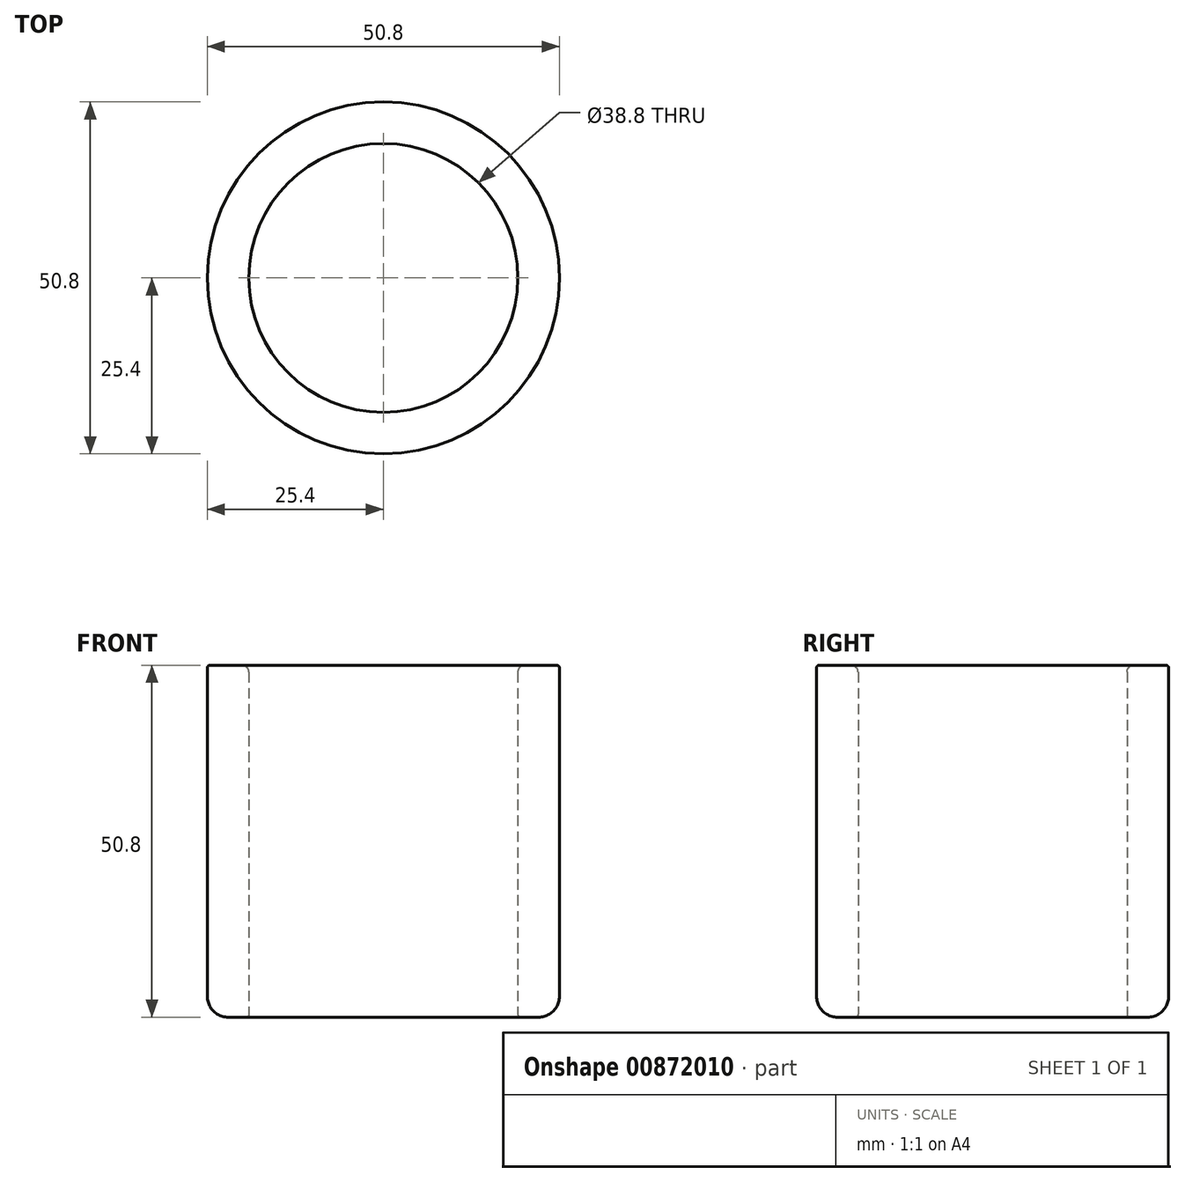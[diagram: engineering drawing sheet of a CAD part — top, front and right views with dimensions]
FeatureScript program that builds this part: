
annotation { "Feature Type Name" : "Feature", "Feature Type Description" : "" }
export const myFeature = defineFeature(function(context is Context, id is Id, definition is map)
    precondition{}
    {
        {
            var Q0;
            Q0=qCreatedBy(makeId("Top.planeOp"),FACE);
            var sketch = newSketch(context, id + "F0", { "sketchPlane" : qUnion([Q0])});
            skCircle(sketch, "E0", {"center": v(0, 0) * mm, "radius": 25.4 * mm});
            skCircle(sketch, "E1", {"center": v(0, 0) * mm, "radius": 19.4 * mm});
            skSolve(sketch);
        }
        {
            var Q0;
            Q0 = qSketchRegion(id + "F0", true);
            extrude(context, id + "F1", {"entities" : qUnion([Q0]), "depth" : 50.8 * mm, "offsetDistance" : 25 * mm});
        }
        {
            var Q0;
            Q0=makeQuery(id+"F1.opExtrude","CAP_EDGE",EDGE,{"disambiguationData":[OSD([sQuery(id+"F0.wireOp",EDGE,"E0")])],"isStart":true});
            fillet(context, id + "F2", {"entities" : qUnion([Q0]), "radius" : 3 * mm, "tangentPropagation" : true, "allowEdgeOverflow" : false});
        }
        {
            var Q0;
            Q0=makeQuery(id+"F1.opExtrude","CAP_EDGE",EDGE,{"disambiguationData":[OSD([sQuery(id+"F0.wireOp",EDGE,"E0")])],"isStart":false});
            var Q1;
            Q1=makeQuery(id+"F1.opExtrude","CAP_EDGE",EDGE,{"disambiguationData":[OSD([sQuery(id+"F0.wireOp",EDGE,"E1")])],"isStart":true});
            fillet(context, id + "F3", {"entities" : qUnion([Q0, Q1]), "radius" : .4 * mm, "tangentPropagation" : true, "allowEdgeOverflow" : false});
        }
        {
            var Q0;
            Q0=makeQuery(id+"F1.opExtrude","CAP_EDGE",EDGE,{"disambiguationData":[OSD([sQuery(id+"F0.wireOp",EDGE,"E1")])],"isStart":false});
            fillet(context, id + "F4", {"entities" : qUnion([Q0]), "radius" : 1 * mm, "tangentPropagation" : true, "allowEdgeOverflow" : false});
        }
    });
